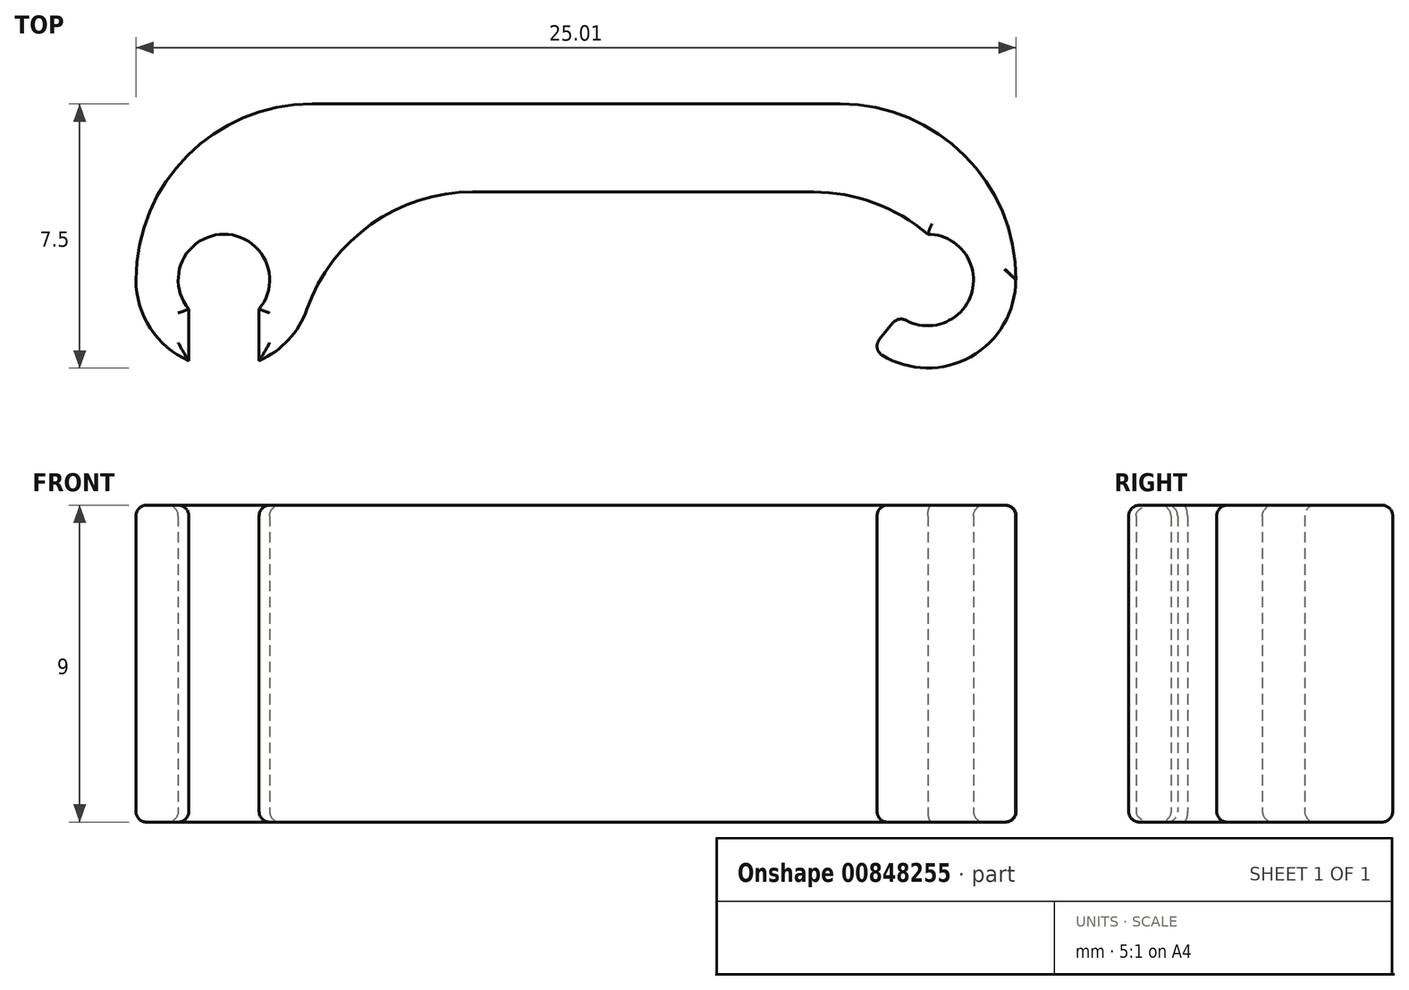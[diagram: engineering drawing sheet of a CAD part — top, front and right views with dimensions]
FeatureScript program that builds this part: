
annotation { "Feature Type Name" : "Feature", "Feature Type Description" : "" }
export const myFeature = defineFeature(function(context is Context, id is Id, definition is map)
    precondition{}
    {
        {
            var Q0;
            Q0=qCreatedBy(makeId("Top.planeOp"),FACE);
            var sketch = newSketch(context, id + "F0", { "sketchPlane" : qUnion([Q0])});
            skArc(sketch, "E0", {"start": v(-2.5, 0) * mm, "mid": v(-2.1, -1.37) * mm, "end": v(-1, -2.3) * mm});
            skArc(sketch, "E1", {"start": v(1, -0.83) * mm, "mid": v(0, 1.3) * mm, "end": v(-1, -0.83) * mm});
            skLineSegment(sketch, "E2", {"start": v(-2.5, 0) * mm, "end": v(-2.5, 5) * mm});
            skLineSegment(sketch, "E3", {"start": v(22.51, 5) * mm, "end": v(22.51, 0) * mm});
            skLineSegment(sketch, "E4", {"start": v(20, 1.3) * mm, "end": v(20, 2.5) * mm});
            skLineSegment(sketch, "E5", {"start": v(20, 2.5) * mm, "end": v(2.5, 2.5) * mm});
            skLineSegment(sketch, "E6", {"start": v(0, 2.5) * mm, "end": v(0, 0) * mm});
            skLineSegment(sketch, "E7", {"start": v(-2.5, 5) * mm, "end": v(22.51, 5) * mm});
            skLineSegment(sketch, "E8", {"start": v(21.3, 0) * mm, "end": v(22.51, 0) * mm});
            skArc(sketch, "E9", {"start": v(18.42, -1.94) * mm, "mid": v(22.36, -0.84) * mm, "end": v(20, 2.5) * mm});
            skArc(sketch, "E10", {"start": v(19.18, -1) * mm, "mid": v(21.23, -0.43) * mm, "end": v(20, 1.3) * mm});
            skLineSegment(sketch, "E11", {"start": v(2.5, 0) * mm, "end": v(2.5, 2.5) * mm});
            skLineSegment(sketch, "E12.left", {"start": v(1, -2.3) * mm, "end": v(1, -0.83) * mm});
            skLineSegment(sketch, "E12.right", {"start": v(-1, -2.3) * mm, "end": v(-1, -0.83) * mm});
            skPoint(sketch, "E13.orphan", {"position": v(-1, 3.1) * mm});
            skPoint(sketch, "E14.orphan", {"position": v(1, 3.1) * mm});
            skPoint(sketch, "E12.bottom.end.orphan", {"position": v(-1, -3.1) * mm});
            skPoint(sketch, "E12.bottom.start.orphan", {"position": v(1, -3.1) * mm});
            skArc(sketch, "E15.trimOffspring", {"start": v(1, -2.3) * mm, "mid": v(2.1, -1.37) * mm, "end": v(2.5, 0) * mm});
            skLineSegment(sketch, "E16", {"start": v(19.18, -1) * mm, "end": v(18.42, -1.94) * mm});
            skPoint(sketch, "E17.start.orphan", {"position": v(17.5, 0) * mm});
            skSolve(sketch);
        }
        {
            var Q0;
            Q0=makeQuery(id+"F0.imprint","IMPRINT",FACE,{"disambiguationData":[TD([[makeQuery(id+"F0.imprint","IMPRINT",EDGE,{"derivedFrom":sQuery(id+"F0.wireOp",EDGE,"E0")}),1.0]])]});
            var Q1;
            {var subQ5=sQuery(id+"F0.wireOp",EDGE,"E16");Q1=makeQuery(id+"F0.imprint","IMPRINT",FACE,{"disambiguationData":[TD([[makeQuery(id+"F0.imprint","IMPRINT",EDGE,{"derivedFrom":subQ5}),1.0]])]});}
            var Q2;
            {var subQ0=sQuery(id+"F0.wireOp",EDGE,"E4");Q2=makeQuery(id+"F0.imprint","IMPRINT",FACE,{"disambiguationData":[TD([[makeQuery(id+"F0.imprint","IMPRINT",EDGE,{"derivedFrom":subQ0}),-1.0]])]});}
            extrude(context, id + "F1", {"entities" : qUnion([Q0, Q1, Q2]), "depth" : 9 * mm, "offsetDistance" : 25 * mm});
        }
        {
            var Q0;
            Q0=makeQuery(id+"F1.opExtrude","SWEPT_EDGE",EDGE,{"disambiguationData":[OSD([sQuery(id+"F0.wireOp",EDGE,"E2"),sQuery(id+"F0.wireOp",EDGE,"E7")])]});
            var Q1;
            Q1=makeQuery(id+"F1.opExtrude","SWEPT_EDGE",EDGE,{"disambiguationData":[OSD([sQuery(id+"F0.wireOp",EDGE,"E5"),sQuery(id+"F0.wireOp",EDGE,"E11")])]});
            var Q2;
            Q2=makeQuery(id+"F1.opExtrude","SWEPT_EDGE",EDGE,{"disambiguationData":[OSD([sQuery(id+"F0.wireOp",EDGE,"E3"),sQuery(id+"F0.wireOp",EDGE,"E7")])]});
            var Q3;
            Q3=makeQuery(id+"F1.opExtrude","SWEPT_EDGE",EDGE,{"disambiguationData":[OSD([sQuery(id+"F0.wireOp",EDGE,"E4"),sQuery(id+"F0.wireOp",EDGE,"E5"),sQuery(id+"F0.wireOp",EDGE,"E9")])]});
            fillet(context, id + "F2", {"entities" : qUnion([Q0, Q1, Q2, Q3]), "radius" : 5 * mm, "tangentPropagation" : true, "allowEdgeOverflow" : false});
        }
        {
            var Q0;
            Q0=makeQuery(id+"F1.opExtrude","CAP_FACE",FACE,{"disambiguationData":[OSD([sQuery(id+"F0.wireOp",EDGE,"E0"),sQuery(id+"F0.wireOp",EDGE,"E1"),sQuery(id+"F0.wireOp",EDGE,"E2"),sQuery(id+"F0.wireOp",EDGE,"E3"),sQuery(id+"F0.wireOp",EDGE,"E4"),sQuery(id+"F0.wireOp",EDGE,"E5"),sQuery(id+"F0.wireOp",EDGE,"E7"),sQuery(id+"F0.wireOp",EDGE,"E8"),sQuery(id+"F0.wireOp",EDGE,"E9"),sQuery(id+"F0.wireOp",EDGE,"E10"),sQuery(id+"F0.wireOp",EDGE,"E11"),sQuery(id+"F0.wireOp",EDGE,"E12.left"),sQuery(id+"F0.wireOp",EDGE,"E12.right"),sQuery(id+"F0.wireOp",EDGE,"E15.trimOffspring"),sQuery(id+"F0.wireOp",EDGE,"E16")])],"isStart":false});
            var Q1;
            Q1=makeQuery(id+"F1.opExtrude","CAP_FACE",FACE,{"disambiguationData":[OSD([sQuery(id+"F0.wireOp",EDGE,"E0"),sQuery(id+"F0.wireOp",EDGE,"E1"),sQuery(id+"F0.wireOp",EDGE,"E2"),sQuery(id+"F0.wireOp",EDGE,"E3"),sQuery(id+"F0.wireOp",EDGE,"E4"),sQuery(id+"F0.wireOp",EDGE,"E5"),sQuery(id+"F0.wireOp",EDGE,"E7"),sQuery(id+"F0.wireOp",EDGE,"E8"),sQuery(id+"F0.wireOp",EDGE,"E9"),sQuery(id+"F0.wireOp",EDGE,"E10"),sQuery(id+"F0.wireOp",EDGE,"E11"),sQuery(id+"F0.wireOp",EDGE,"E12.left"),sQuery(id+"F0.wireOp",EDGE,"E12.right"),sQuery(id+"F0.wireOp",EDGE,"E15.trimOffspring"),sQuery(id+"F0.wireOp",EDGE,"E16")])],"isStart":true});
            var Q2;
            Q2=makeQuery(id+"F1.opExtrude","SWEPT_FACE",FACE,{"disambiguationData":[OSD([sQuery(id+"F0.wireOp",EDGE,"E16")])]});
            fillet(context, id + "F3", {"entities" : qUnion([Q0, Q1, Q2]), "radius" : 0.3 * mm, "tangentPropagation" : true, "allowEdgeOverflow" : false});
        }
    });
